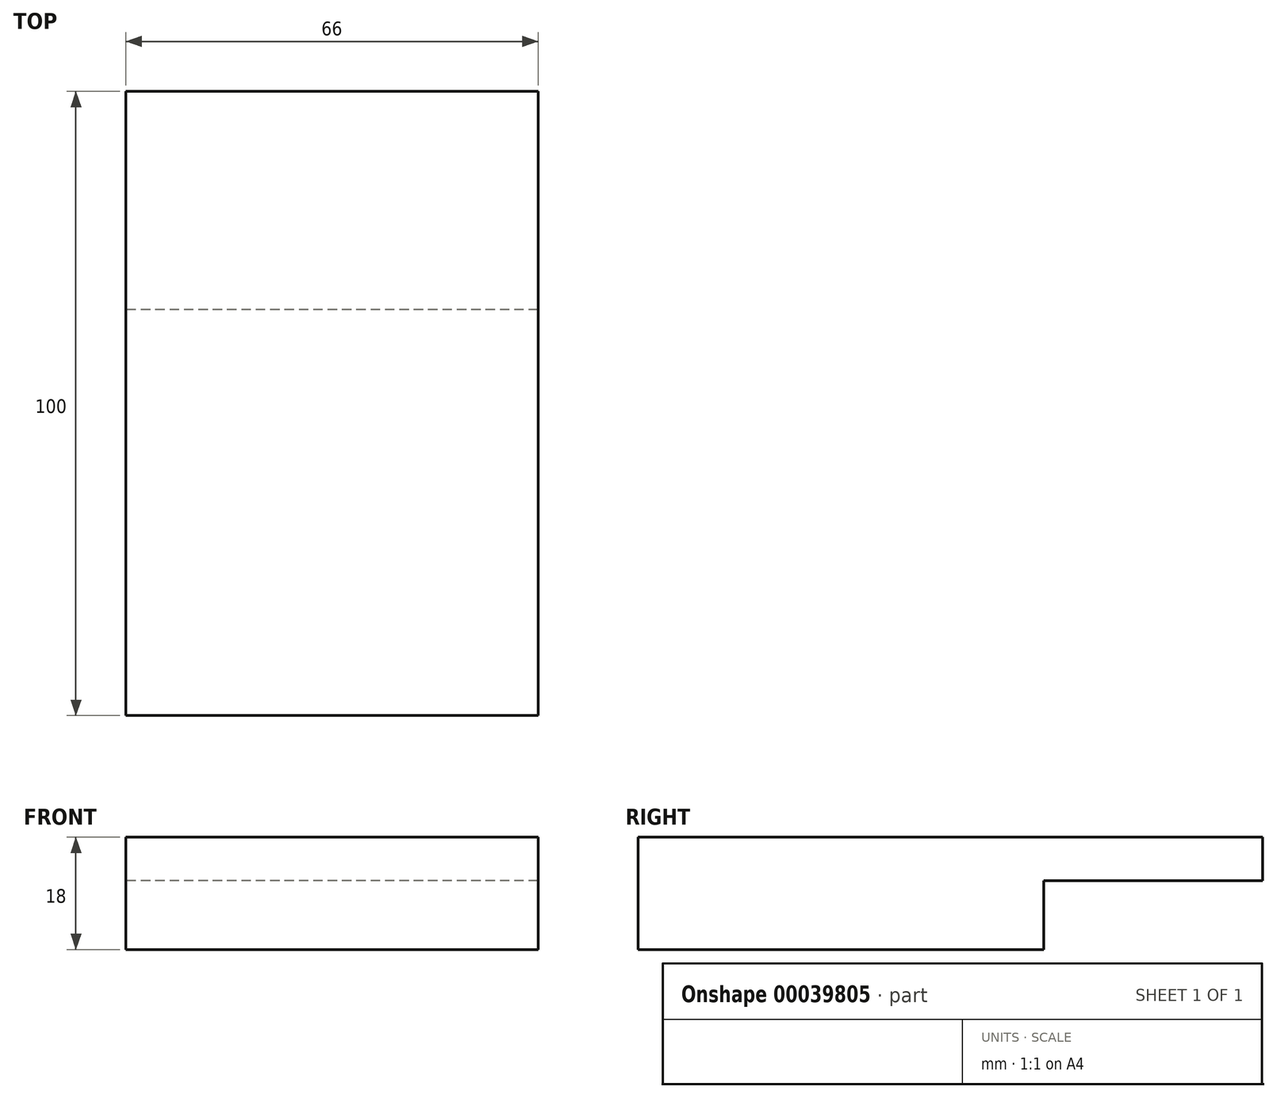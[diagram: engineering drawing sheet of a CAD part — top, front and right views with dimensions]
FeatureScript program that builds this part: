
annotation { "Feature Type Name" : "Feature", "Feature Type Description" : "" }
export const myFeature = defineFeature(function(context is Context, id is Id, definition is map)
    precondition{}
    {
        {
            var Q0;
            Q0=qCreatedBy(makeId("Right.planeOp"),FACE);
            var sketch = newSketch(context, id + "F0", { "sketchPlane" : qUnion([Q0])});
            skLineSegment(sketch, "E0", {"start": v(-26.84, 33.18) * mm, "end": v(73.16, 33.18) * mm});
            skLineSegment(sketch, "E1", {"start": v(73.16, 33.18) * mm, "end": v(73.16, 26.18) * mm});
            skLineSegment(sketch, "E2", {"start": v(73.16, 26.18) * mm, "end": v(38.16, 26.18) * mm});
            skLineSegment(sketch, "E3", {"start": v(38.16, 26.18) * mm, "end": v(38.16, 15.18) * mm});
            skLineSegment(sketch, "E4", {"start": v(38.16, 15.18) * mm, "end": v(-26.84, 15.18) * mm});
            skLineSegment(sketch, "E5", {"start": v(-26.84, 15.18) * mm, "end": v(-26.84, 33.18) * mm});
            skSolve(sketch);
        }
        {
            var Q0;
            Q0=makeQuery(id+"F0.imprint","IMPRINT",FACE,{"disambiguationData":[TD([[makeQuery(id+"F0.imprint","IMPRINT",EDGE,{"derivedFrom":sQuery(id+"F0.wireOp",EDGE,"E0")}),-1.0]])]});
            extrude(context, id + "F1", {"entities" : qUnion([Q0]), "depth" : 66 * mm});
        }
    });
